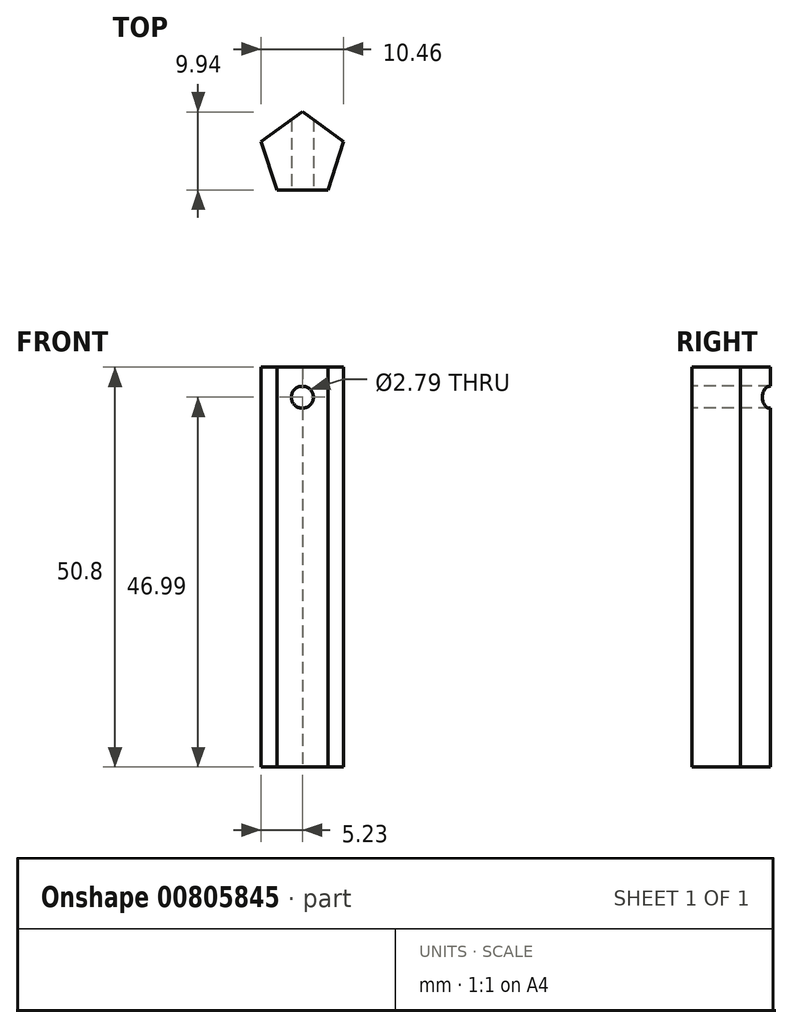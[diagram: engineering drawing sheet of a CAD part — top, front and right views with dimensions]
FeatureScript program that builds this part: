
annotation { "Feature Type Name" : "Feature", "Feature Type Description" : "" }
export const myFeature = defineFeature(function(context is Context, id is Id, definition is map)
    precondition{}
    {
        {
            var Q0;
            Q0=qCreatedBy(makeId("Top.planeOp"),FACE);
            var sketch = newSketch(context, id + "F0", { "sketchPlane" : qUnion([Q0])});
            skCircle(sketch, "E0.cCircle", {"center": v(0, 0) * mm, "radius": 4.45 * mm, "construction": true});
            skLineSegment(sketch, "E0.0", {"start": v(5.23, 1.7) * mm, "end": v(3.23, -4.45) * mm});
            skLineSegment(sketch, "E0.1", {"start": v(3.23, -4.45) * mm, "end": v(-3.23, -4.45) * mm});
            skLineSegment(sketch, "E0.2", {"start": v(-3.23, -4.45) * mm, "end": v(-5.23, 1.7) * mm});
            skLineSegment(sketch, "E0.3", {"start": v(-5.23, 1.7) * mm, "end": v(0, 5.5) * mm});
            skLineSegment(sketch, "E0.4", {"start": v(0, 5.5) * mm, "end": v(5.23, 1.7) * mm});
            skPoint(sketch, "E0.0.midPoint", {"position": v(4.23, -1.37) * mm});
            skSolve(sketch);
        }
        {
            var Q0;
            Q0 = qSketchRegion(id + "F0", true);
            extrude(context, id + "F1", {"entities" : qUnion([Q0]), "depth" : 50.8 * mm, "offsetDistance" : 25.4 * mm});
        }
        {
            var Q0;
            Q0=makeQuery(id+"F1.opExtrude","SWEPT_FACE",FACE,{"disambiguationData":[OSD([sQuery(id+"F0.wireOp",EDGE,"E0.1")])]});
            var sketch = newSketch(context, id + "F2", { "sketchPlane" : qUnion([Q0])});
            skCircle(sketch, "E1", {"center": v(0, 47) * mm, "radius": 1.4 * mm});
            skSolve(sketch);
        }
        {
            var Q0;
            Q0 = qSketchRegion(id + "F2", true);
            extrude(context, id + "F3", {"entities" : qUnion([Q0]), "operationType" : NewBodyOperationType.REMOVE, "endBound" : BoundingType.SYMMETRIC, "oppositeDirection" : true, "depth" : 127 * mm, "offsetDistance" : 25.4 * mm});
        }
    });
